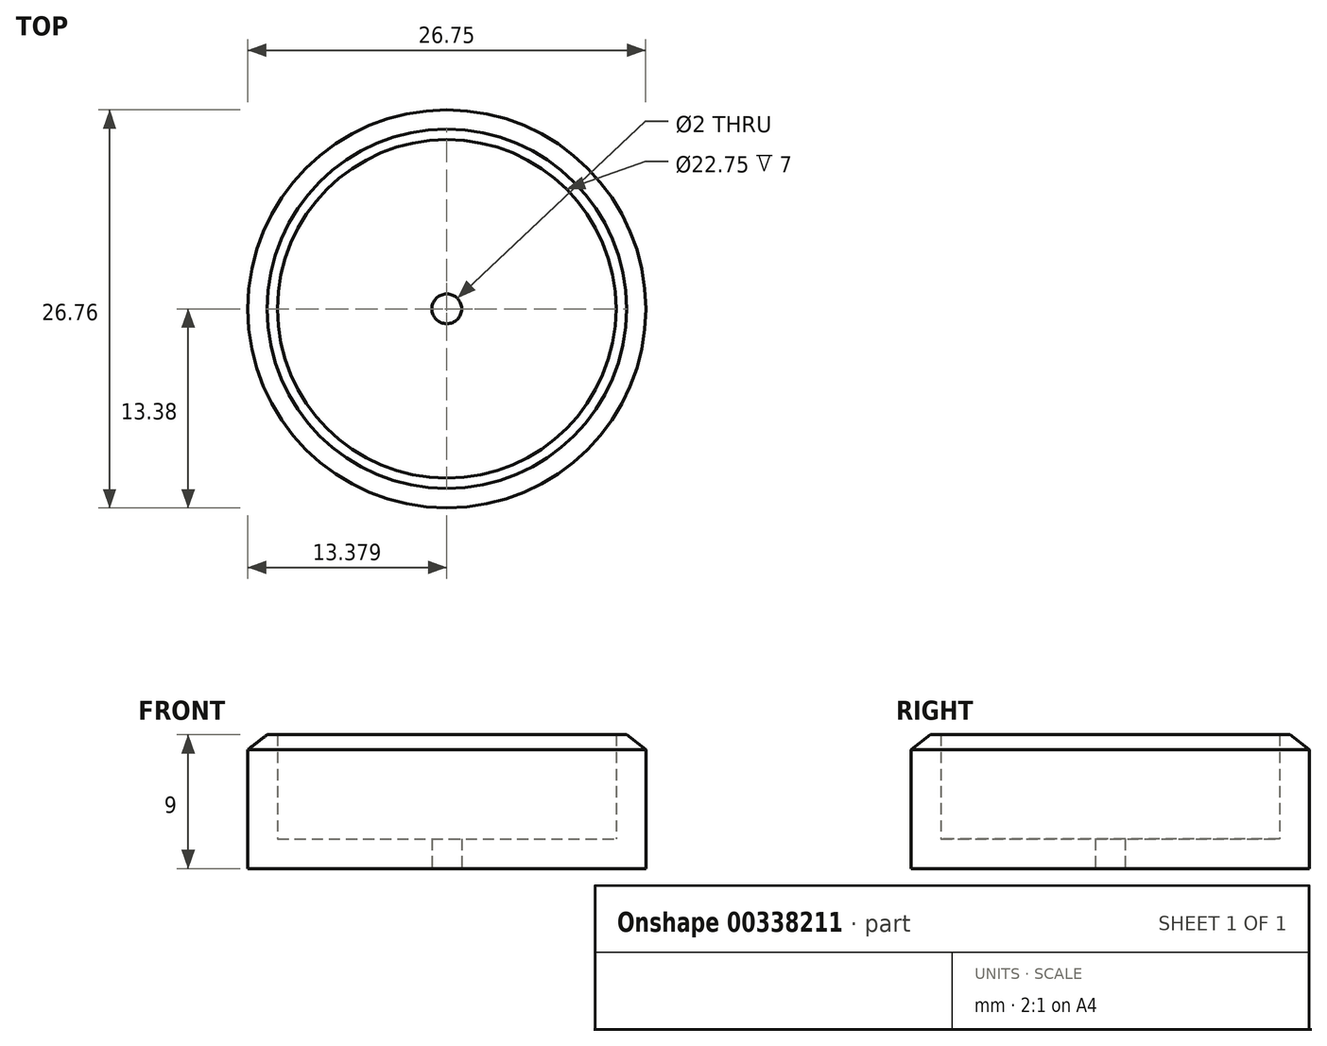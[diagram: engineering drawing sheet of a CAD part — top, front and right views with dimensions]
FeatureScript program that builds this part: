
annotation { "Feature Type Name" : "Feature", "Feature Type Description" : "" }
export const myFeature = defineFeature(function(context is Context, id is Id, definition is map)
    precondition{}
    {
        {
            var Q0;
            Q0=qCreatedBy(makeId("Front.planeOp"),FACE);
            var sketch = newSketch(context, id + "F0", { "sketchPlane" : qUnion([Q0])});
            skLineSegment(sketch, "E0", {"start": v(3.82, -2.03) * mm, "end": v(3.82, -0.03) * mm, "construction": true});
            skLineSegment(sketch, "E1", {"start": v(3.82, -2.03) * mm, "end": v(2.82, -2.03) * mm, "construction": true});
            skLineSegment(sketch, "E2", {"start": v(2.82, -2.03) * mm, "end": v(2.82, -0.03) * mm, "construction": true});
            skLineSegment(sketch, "E3", {"start": v(2.82, -0.03) * mm, "end": v(3.82, -0.03) * mm, "construction": true});
            skLineSegment(sketch, "E4", {"start": v(2.82, -2.03) * mm, "end": v(-9.56, -2.03) * mm});
            skLineSegment(sketch, "E5", {"start": v(2.82, -0.03) * mm, "end": v(-7.56, -0.03) * mm});
            skLineSegment(sketch, "E6", {"start": v(-9.56, 5.97) * mm, "end": v(-9.56, -2.03) * mm});
            skLineSegment(sketch, "E7", {"start": v(-9.56, 5.97) * mm, "end": v(-8.26, 6.97) * mm});
            skLineSegment(sketch, "E8", {"start": v(-8.26, 6.97) * mm, "end": v(-7.56, 6.97) * mm});
            skLineSegment(sketch, "E9", {"start": v(2.82, -0.03) * mm, "end": v(2.82, -2.03) * mm});
            skPoint(sketch, "E10.end.orphan", {"position": v(-7.56, 5.97) * mm});
            skLineSegment(sketch, "E11", {"start": v(-7.56, -0.03) * mm, "end": v(-7.56, 6.97) * mm});
            skSolve(sketch);
        }
        {
            var Q0;
            Q0 = qSketchRegion(id + "F0", true);
            var Q1;
            Q1=sQuery(id+"F0.wireOp",EDGE,"E0");
            revolve(context, id + "F1", {"entities" : qUnion([Q0]), "axis" : qUnion([Q1]), "revolveType" : RevolveType.FULL});
        }
    });
